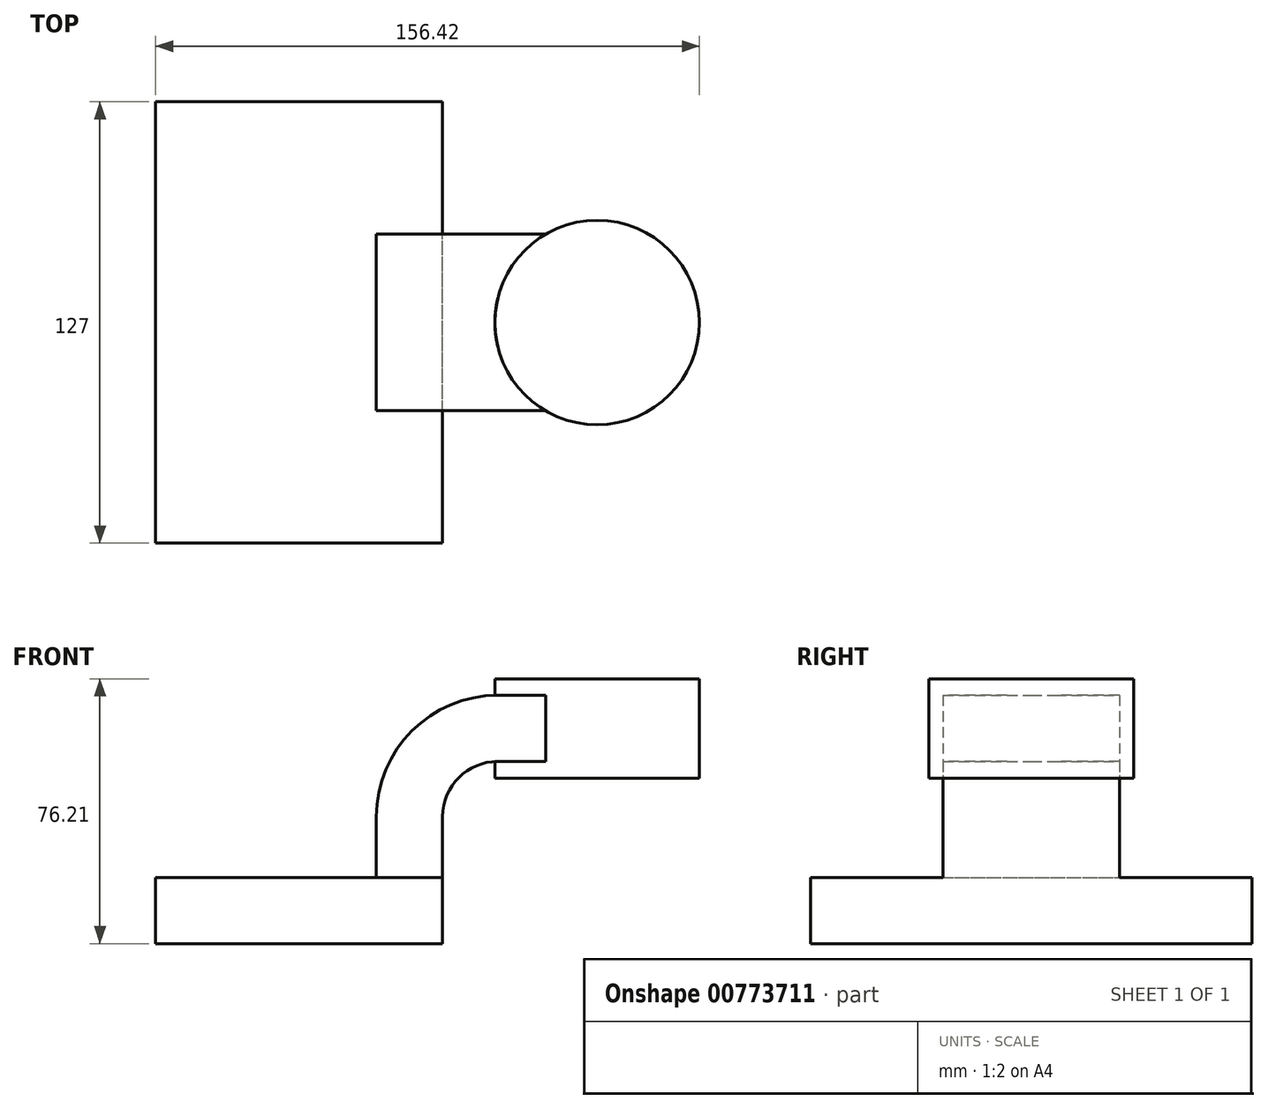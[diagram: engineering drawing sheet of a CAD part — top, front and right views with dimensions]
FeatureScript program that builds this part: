
annotation { "Feature Type Name" : "Feature", "Feature Type Description" : "" }
export const myFeature = defineFeature(function(context is Context, id is Id, definition is map)
    precondition{}
    {
        {
            var Q0;
            Q0=qCreatedBy(makeId("Front.planeOp"),FACE);
            var sketch = newSketch(context, id + "F0", { "sketchPlane" : qUnion([Q0])});
            skLineSegment(sketch, "E0.bottom", {"start": v(-41.28, -9.52) * mm, "end": v(41.28, -9.52) * mm});
            skLineSegment(sketch, "E0.top", {"start": v(-41.28, 9.52) * mm, "end": v(41.28, 9.52) * mm});
            skLineSegment(sketch, "E0.left", {"start": v(-41.28, -9.52) * mm, "end": v(-41.28, 9.52) * mm});
            skLineSegment(sketch, "E0.right", {"start": v(41.28, -9.52) * mm, "end": v(41.28, 9.52) * mm});
            skPoint(sketch, "E0.middle", {"position": v(0, 0) * mm});
            skLineSegment(sketch, "E1.bottom", {"start": v(115.14, 38.1) * mm, "end": v(64.34, 38.1) * mm});
            skLineSegment(sketch, "E1.top", {"start": v(115.14, 66.68) * mm, "end": v(64.34, 66.68) * mm});
            skLineSegment(sketch, "E1.left", {"start": v(115.14, 38.1) * mm, "end": v(115.14, 66.68) * mm});
            skLineSegment(sketch, "E1.right", {"start": v(64.34, 38.1) * mm, "end": v(64.34, 66.68) * mm});
            skPoint(sketch, "E1.middle", {"position": v(89.74, 52.39) * mm});
            skLineSegment(sketch, "E2", {"start": v(41.27, 9.52) * mm, "end": v(41.27, 27) * mm});
            skArc(sketch, "E3", {"start": v(41.27, 27) * mm, "mid": v(45.92, 38.23) * mm, "end": v(57.15, 42.88) * mm});
            skLineSegment(sketch, "E4", {"start": v(57.15, 42.88) * mm, "end": v(85.72, 42.88) * mm});
            skLineSegment(sketch, "E5.0", {"start": v(57.15, 61.93) * mm, "end": v(85.72, 61.93) * mm});
            skArc(sketch, "E5.1", {"start": v(22.23, 27) * mm, "mid": v(32.45, 51.7) * mm, "end": v(57.15, 61.93) * mm});
            skLineSegment(sketch, "E5.2", {"start": v(22.22, 9.52) * mm, "end": v(22.22, 27) * mm});
            skLineSegment(sketch, "E6", {"start": v(85.72, 38.1) * mm, "end": v(85.72, 66.67) * mm});
            skFitSpline(sketch, "E7", {"points": [v(-41.28, 9.53) * mm, v(57.15, 61.93) * mm], "startDerivative": vector(0.43, 46.3) * mm, "endDerivative": vector(117, -0.5) * mm});
            skSolve(sketch);
        }
        {
            var Q0;
            Q0=makeQuery(id+"F0.imprint","IMPRINT",FACE,{"disambiguationData":[TD([[makeQuery(id+"F0.imprint","IMPRINT",EDGE,{"derivedFrom":sQuery(id+"F0.wireOp",EDGE,"E0.bottom")}),1.0]])]});
            extrude(context, id + "F1", {"entities" : qUnion([Q0]), "endBound" : BoundingType.SYMMETRIC, "depth" : 127 * mm, "offsetDistance" : 25.4 * mm});
        }
        {
            var Q0;
            {var subQ1=sQuery(id+"F0.wireOp",EDGE,"E2");Q0=makeQuery(id+"F0.imprint","IMPRINT",FACE,{"disambiguationData":[TD([[makeQuery(id+"F0.imprint","IMPRINT",EDGE,{"derivedFrom":subQ1}),1.0]])]});}
            var Q1;
            {var subQ0=sQuery(id+"F0.wireOp",EDGE,"E4");var subQ1=sQuery(id+"F0.wireOp",EDGE,"E1.right");var subQ2=makeQuery(id+"F0.imprint","INTERSECT",VERTEX,{"derivedFrom":[subQ1,subQ0]});Q1=makeQuery(id+"F0.imprint","IMPRINT",FACE,{"disambiguationData":[TD([[makeQuery(id+"F0.imprint","IMPRINT",EDGE,{"disambiguationData":[TD([[subQ2,-1.0]])],"derivedFrom":subQ1}),-1.0]])]});}
            extrude(context, id + "F2", {"entities" : qUnion([Q0, Q1]), "operationType" : NewBodyOperationType.ADD, "endBound" : BoundingType.SYMMETRIC, "depth" : 50.8 * mm, "offsetDistance" : 25.4 * mm});
        }
        {
            var Q0;
            Q0=makeQuery(id+"F0.imprint","IMPRINT",FACE,{"disambiguationData":[TD([[makeQuery(id+"F0.imprint","IMPRINT",EDGE,{"derivedFrom":sQuery(id+"F0.wireOp",EDGE,"E5.1")}),1.0]])]});
            extrude(context, id + "F3", {"entities" : qUnion([Q0]), "operationType" : NewBodyOperationType.ADD, "endBound" : BoundingType.SYMMETRIC, "depth" : 15.88 * mm, "offsetDistance" : 25.4 * mm});
        }
        {
            var Q0;
            {var subQ4=sQuery(id+"F0.wireOp",EDGE,"E1.left");Q0=makeQuery(id+"F0.imprint","IMPRINT",FACE,{"disambiguationData":[TD([[makeQuery(id+"F0.imprint","IMPRINT",EDGE,{"derivedFrom":subQ4}),1.0]])]});}
            var Q1;
            Q1=sQuery(id+"F0.wireOp",EDGE,"E6");
            revolve(context, id + "F4", {"operationType" : NewBodyOperationType.ADD, "surfaceOperationType" : NewSurfaceOperationType.NEW, "entities" : qUnion([Q0]), "axis" : qUnion([Q1]), "revolveType" : RevolveType.FULL});
        }
    });
